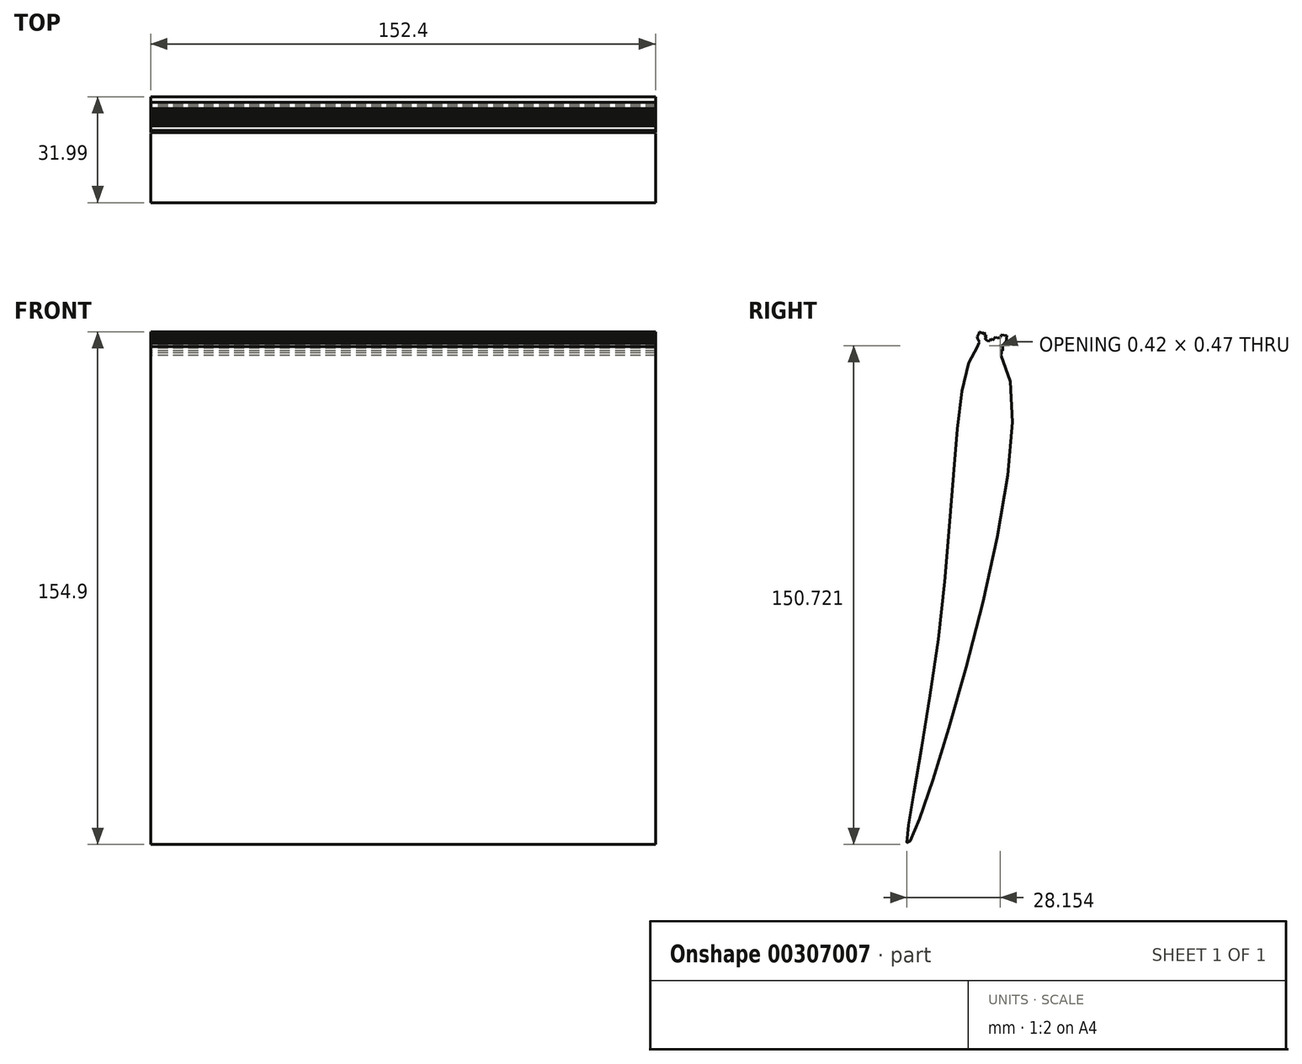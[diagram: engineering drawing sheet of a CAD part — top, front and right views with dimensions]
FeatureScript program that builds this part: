
annotation { "Feature Type Name" : "Feature", "Feature Type Description" : "" }
export const myFeature = defineFeature(function(context is Context, id is Id, definition is map)
    precondition{}
    {
        {
            var Q0;
            Q0=qCreatedBy(makeId("Right.planeOp"),FACE);
            var sketch = newSketch(context, id + "F0", { "sketchPlane" : qUnion([Q0])});
            skFitSpline(sketch, "E0", {"points": [v(19.1, 73.86) * mm, v(28.95, 59.3) * mm, v(-2.03, -76.46) * mm, v(7.39, -9.42) * mm, v(19.1, 73.86) * mm]});
            skLineSegment(sketch, "E1", {"start": v(23.21, 73.66) * mm, "end": v(25.8, 76.18) * mm});
            skLineSegment(sketch, "E2", {"start": v(25.8, 76.18) * mm, "end": v(26.77, 75.32) * mm});
            skLineSegment(sketch, "E3", {"start": v(26.77, 75.32) * mm, "end": v(24.37, 72.66) * mm});
            skLineSegment(sketch, "E4", {"start": v(24.37, 72.66) * mm, "end": v(23.21, 73.66) * mm});
            skLineSegment(sketch, "E5", {"start": v(25.8, 76.18) * mm, "end": v(26.45, 76.9) * mm});
            skPoint(sketch, "E5.endSnap0", {"position": v(26.29, 75.75) * mm});
            skLineSegment(sketch, "E6", {"start": v(26.45, 76.9) * mm, "end": v(27.35, 75.97) * mm});
            skLineSegment(sketch, "E7", {"start": v(27.35, 75.97) * mm, "end": v(26.77, 75.32) * mm});
            skLineSegment(sketch, "E8", {"start": v(20.8, 74.43) * mm, "end": v(20.13, 76.98) * mm});
            skLineSegment(sketch, "E9", {"start": v(20.13, 76.98) * mm, "end": v(18.88, 76.65) * mm});
            skLineSegment(sketch, "E10", {"start": v(18.88, 76.65) * mm, "end": v(19.55, 74.12) * mm});
            skLineSegment(sketch, "E11", {"start": v(19.55, 74.12) * mm, "end": v(20.8, 74.43) * mm});
            skLineSegment(sketch, "E12", {"start": v(24.94, 72.1) * mm, "end": v(25.14, 73.52) * mm});
            skLineSegment(sketch, "E13", {"start": v(25.14, 73.52) * mm, "end": v(25.57, 73.99) * mm});
            skLineSegment(sketch, "E14", {"start": v(25.57, 73.99) * mm, "end": v(25.53, 73.73) * mm});
            skPoint(sketch, "E14.endSnap0", {"position": v(25.35, 73.75) * mm});
            skLineSegment(sketch, "E15", {"start": v(25.53, 73.73) * mm, "end": v(25.14, 73.52) * mm});
            skLineSegment(sketch, "E16", {"start": v(25.04, 72.8) * mm, "end": v(25.73, 73.57) * mm});
            skLineSegment(sketch, "E17", {"start": v(25.73, 73.57) * mm, "end": v(25.83, 74.27) * mm});
            skLineSegment(sketch, "E18", {"start": v(25.83, 74.27) * mm, "end": v(26.25, 73.9) * mm});
            skLineSegment(sketch, "E19", {"start": v(26.25, 73.9) * mm, "end": v(25.73, 73.57) * mm});
            skLineSegment(sketch, "E20", {"start": v(26.43, 74.95) * mm, "end": v(27.27, 74.83) * mm});
            skLineSegment(sketch, "E21", {"start": v(27.27, 74.83) * mm, "end": v(26.77, 75.32) * mm});
            skLineSegment(sketch, "E22", {"start": v(27.35, 75.97) * mm, "end": v(27.33, 75.24) * mm});
            skLineSegment(sketch, "E23", {"start": v(27.33, 75.24) * mm, "end": v(26.65, 74.48) * mm});
            skLineSegment(sketch, "E24", {"start": v(26.65, 74.48) * mm, "end": v(25.83, 74.27) * mm});
            skLineSegment(sketch, "E25", {"start": v(26.65, 74.48) * mm, "end": v(26.6, 74.17) * mm});
            skLineSegment(sketch, "E26", {"start": v(26.6, 74.17) * mm, "end": v(26.25, 73.9) * mm});
            skLineSegment(sketch, "E27", {"start": v(27.33, 75.24) * mm, "end": v(26.77, 75.32) * mm});
            skLineSegment(sketch, "E28", {"start": v(26.25, 73.9) * mm, "end": v(26.1, 72.93) * mm});
            skLineSegment(sketch, "E29", {"start": v(26.1, 72.93) * mm, "end": v(25.04, 72.8) * mm});
            skLineSegment(sketch, "E30", {"start": v(27.35, 75.97) * mm, "end": v(27.46, 76.75) * mm});
            skLineSegment(sketch, "E31", {"start": v(27.46, 76.75) * mm, "end": v(27.04, 76.29) * mm});
            skLineSegment(sketch, "E32", {"start": v(27.04, 76.29) * mm, "end": v(27.46, 76.75) * mm});
            skLineSegment(sketch, "E33", {"start": v(27.46, 76.75) * mm, "end": v(26.45, 76.9) * mm});
            skLineSegment(sketch, "E34", {"start": v(26.45, 76.9) * mm, "end": v(25.63, 77) * mm});
            skLineSegment(sketch, "E35", {"start": v(25.63, 77) * mm, "end": v(25.52, 76.22) * mm});
            skLineSegment(sketch, "E36", {"start": v(25.52, 76.22) * mm, "end": v(24.54, 76) * mm});
            skLineSegment(sketch, "E37", {"start": v(24.54, 76) * mm, "end": v(24.06, 76.43) * mm});
            skLineSegment(sketch, "E38", {"start": v(24.06, 76.43) * mm, "end": v(23.9, 75.3) * mm});
            skLineSegment(sketch, "E39", {"start": v(23.9, 75.3) * mm, "end": v(23.84, 74.88) * mm});
            skLineSegment(sketch, "E40", {"start": v(23.84, 74.88) * mm, "end": v(23.1, 74.8) * mm});
            skLineSegment(sketch, "E41", {"start": v(23.1, 74.8) * mm, "end": v(22.98, 73.91) * mm});
            skLineSegment(sketch, "E42", {"start": v(22.98, 73.91) * mm, "end": v(23.21, 73.66) * mm});
            skLineSegment(sketch, "E43", {"start": v(24.06, 76.43) * mm, "end": v(23.14, 75.41) * mm});
            skLineSegment(sketch, "E44", {"start": v(23.14, 75.41) * mm, "end": v(22.6, 75.9) * mm});
            skLineSegment(sketch, "E45", {"start": v(22.6, 75.9) * mm, "end": v(22.24, 75.1) * mm});
            skLineSegment(sketch, "E46", {"start": v(22.24, 75.1) * mm, "end": v(21.53, 75.2) * mm});
            skLineSegment(sketch, "E47", {"start": v(21.53, 75.2) * mm, "end": v(21, 74.6) * mm});
            skLineSegment(sketch, "E48", {"start": v(21.53, 75.2) * mm, "end": v(20.95, 75.72) * mm});
            skLineSegment(sketch, "E49", {"start": v(20.95, 75.72) * mm, "end": v(20.6, 75.33) * mm});
            skLineSegment(sketch, "E50", {"start": v(20.6, 75.33) * mm, "end": v(20.72, 76.17) * mm});
            skLineSegment(sketch, "E51", {"start": v(20.72, 76.17) * mm, "end": v(20.24, 76.6) * mm});
            skLineSegment(sketch, "E52", {"start": v(20.24, 76.6) * mm, "end": v(20.13, 76.98) * mm});
            skLineSegment(sketch, "E53", {"start": v(20.72, 76.17) * mm, "end": v(20.82, 76.88) * mm});
            skLineSegment(sketch, "E54", {"start": v(20.82, 76.88) * mm, "end": v(20.24, 76.6) * mm});
            skLineSegment(sketch, "E55", {"start": v(20.82, 76.88) * mm, "end": v(21.3, 76.45) * mm});
            skLineSegment(sketch, "E56", {"start": v(21.3, 76.45) * mm, "end": v(20.72, 76.17) * mm});
            skLineSegment(sketch, "E57", {"start": v(20.82, 76.88) * mm, "end": v(20.6, 77.72) * mm});
            skLineSegment(sketch, "E58", {"start": v(20.6, 77.72) * mm, "end": v(20.13, 76.98) * mm});
            skLineSegment(sketch, "E59", {"start": v(20.13, 76.98) * mm, "end": v(19.6, 77.46) * mm});
            skPoint(sketch, "E59.endSnap0", {"position": v(19.5, 76.81) * mm});
            skLineSegment(sketch, "E60", {"start": v(19.6, 77.46) * mm, "end": v(18.88, 76.65) * mm});
            skLineSegment(sketch, "E61", {"start": v(18.88, 76.65) * mm, "end": v(19.06, 77.93) * mm});
            skLineSegment(sketch, "E62", {"start": v(19.06, 77.93) * mm, "end": v(20.37, 77.35) * mm});
            skLineSegment(sketch, "E63", {"start": v(20.37, 77.35) * mm, "end": v(20.6, 77.72) * mm});
            skLineSegment(sketch, "E64", {"start": v(18.95, 77.15) * mm, "end": v(18.36, 76.5) * mm});
            skLineSegment(sketch, "E65", {"start": v(18.36, 76.5) * mm, "end": v(19.28, 75.2) * mm});
            skLineSegment(sketch, "E66", {"start": v(19.28, 75.2) * mm, "end": v(18.63, 75.61) * mm});
            skLineSegment(sketch, "E67", {"start": v(18.63, 75.61) * mm, "end": v(18.5, 76.06) * mm});
            skLineSegment(sketch, "E68", {"start": v(18.5, 76.06) * mm, "end": v(18.36, 76.5) * mm});
            skLineSegment(sketch, "E69", {"start": v(19.55, 74.12) * mm, "end": v(19.1, 73.86) * mm});
            skLineSegment(sketch, "E70", {"start": v(19.1, 73.86) * mm, "end": v(18.92, 74.52) * mm});
            skLineSegment(sketch, "E71", {"start": v(18.92, 74.52) * mm, "end": v(19.34, 75.1) * mm});
            skLineSegment(sketch, "E72", {"start": v(19.34, 75.1) * mm, "end": v(18.63, 75.61) * mm});
            skLineSegment(sketch, "E73", {"start": v(18.63, 75.61) * mm, "end": v(19.13, 74.81) * mm});
            skLineSegment(sketch, "E74", {"start": v(26.1, 72.93) * mm, "end": v(26.19, 72.23) * mm});
            skLineSegment(sketch, "E75", {"start": v(26.19, 72.23) * mm, "end": v(25.67, 72.12) * mm});
            skLineSegment(sketch, "E76", {"start": v(25.67, 72.12) * mm, "end": v(25.82, 71.5) * mm});
            skLineSegment(sketch, "E77", {"start": v(25.82, 71.5) * mm, "end": v(25.72, 70.84) * mm});
            skLineSegment(sketch, "E78", {"start": v(25.72, 70.84) * mm, "end": v(24.94, 72.1) * mm});
            skLineSegment(sketch, "E79", {"start": v(18.92, 74.52) * mm, "end": v(18.53, 73.4) * mm});
            skLineSegment(sketch, "E80", {"start": v(18.53, 73.4) * mm, "end": v(19.1, 73.86) * mm});
            skLineSegment(sketch, "E81", {"start": v(20.72, 76.17) * mm, "end": v(20.95, 75.72) * mm});
            skLineSegment(sketch, "E82.0", {"start": v(18.92, 74.52) * mm, "end": v(25.73, 73.57) * mm, "construction": true});
            skLineSegment(sketch, "E83.0", {"start": v(18.5, 76.06) * mm, "end": v(27.27, 74.83) * mm, "construction": true});
            skLineSegment(sketch, "E84.0", {"start": v(18.63, 75.61) * mm, "end": v(21.53, 75.2) * mm, "construction": true});
            skLineSegment(sketch, "E85.0", {"start": v(19.28, 75.2) * mm, "end": v(26.6, 74.17) * mm, "construction": true});
            skLineSegment(sketch, "E86.0", {"start": v(18.36, 76.5) * mm, "end": v(27.33, 75.24) * mm, "construction": true});
            skLineSegment(sketch, "E87.0", {"start": v(19.06, 77.93) * mm, "end": v(27.46, 76.75) * mm, "construction": true});
            skLineSegment(sketch, "E88.0", {"start": v(18.95, 77.15) * mm, "end": v(27.35, 75.97) * mm, "construction": true});
            skLineSegment(sketch, "E89.0", {"start": v(20.24, 76.6) * mm, "end": v(26.29, 75.75) * mm, "construction": true});
            skLineSegment(sketch, "E90.0", {"start": v(25.35, 73.75) * mm, "end": v(25.53, 73.73) * mm, "construction": true});
            skLineSegment(sketch, "E91.0", {"start": v(23.14, 75.41) * mm, "end": v(23.9, 75.3) * mm, "construction": true});
            skLineSegment(sketch, "E92.0", {"start": v(23.84, 74.88) * mm, "end": v(26.65, 74.48) * mm, "construction": true});
            skLineSegment(sketch, "E93.0", {"start": v(19.28, 75.2) * mm, "end": v(19.6, 77.46) * mm, "construction": true});
            skLineSegment(sketch, "E94.0", {"start": v(26.65, 74.48) * mm, "end": v(26.77, 75.32) * mm, "construction": true});
            skLineSegment(sketch, "E95.0", {"start": v(18.88, 76.65) * mm, "end": v(18.95, 77.15) * mm, "construction": true});
            skLineSegment(sketch, "E96.0", {"start": v(26.29, 75.75) * mm, "end": v(26.45, 76.9) * mm, "construction": true});
            skLineSegment(sketch, "E97.0", {"start": v(25.04, 72.8) * mm, "end": v(25.63, 77) * mm, "construction": true});
            skLineSegment(sketch, "E98.0", {"start": v(27.27, 74.83) * mm, "end": v(27.33, 75.24) * mm, "construction": true});
            skSolve(sketch);
        }
        {
            var Q0;
            Q0=qSketchRegion(id+"F0",true);
            var Q1;
            Q1=makeQuery(id+"F0.imprint","IMPRINT",FACE,{"disambiguationData":[TD([[makeQuery(id+"F0.imprint","IMPRINT",EDGE,{"derivedFrom":sQuery(id+"F0.wireOp",EDGE,"E1")}),1.0]])]});
            var Q2;
            {var subQ3=sQuery(id+"F0.wireOp",EDGE,"E1");Q2=makeQuery(id+"F0.imprint","IMPRINT",FACE,{"disambiguationData":[TD([[makeQuery(id+"F0.imprint","IMPRINT",EDGE,{"derivedFrom":subQ3}),-1.0]])]});}
            var Q3;
            {var subQ0=sQuery(id+"F0.wireOp",EDGE,"E29");Q3=makeQuery(id+"F0.imprint","IMPRINT",FACE,{"disambiguationData":[TD([[makeQuery(id+"F0.imprint","IMPRINT",EDGE,{"derivedFrom":subQ0}),1.0]])]});}
            var Q4;
            {var subQ0=sQuery(id+"F0.wireOp",EDGE,"E78");var subQ1=sQuery(id+"F0.wireOp",EDGE,"E12");var subQ2=makeQuery(id+"F0.imprint","INTERSECT",VERTEX,{"derivedFrom":[subQ1,subQ0]});Q4=makeQuery(id+"F0.imprint","IMPRINT",FACE,{"disambiguationData":[TD([[makeQuery(id+"F0.imprint","IMPRINT",EDGE,{"disambiguationData":[TD([[subQ2,1.0]])],"derivedFrom":subQ0}),1.0]])]});}
            var Q5;
            {var subQ2=sQuery(id+"F0.wireOp",EDGE,"E8");Q5=makeQuery(id+"F0.imprint","IMPRINT",FACE,{"disambiguationData":[TD([[makeQuery(id+"F0.imprint","IMPRINT",EDGE,{"derivedFrom":subQ2}),-1.0]])]});}
            var Q6;
            {var subQ0=sQuery(id+"F0.wireOp",EDGE,"E11");Q6=makeQuery(id+"F0.imprint","IMPRINT",FACE,{"disambiguationData":[TD([[makeQuery(id+"F0.imprint","IMPRINT",EDGE,{"derivedFrom":subQ0}),1.0]])]});}
            var Q7;
            {var subQ0=sQuery(id+"F0.wireOp",EDGE,"E4");Q7=makeQuery(id+"F0.imprint","IMPRINT",FACE,{"disambiguationData":[TD([[makeQuery(id+"F0.imprint","IMPRINT",EDGE,{"derivedFrom":subQ0}),-1.0]])]});}
            var Q8;
            {var subQ0=sQuery(id+"F0.wireOp",EDGE,"E78");var subQ1=sQuery(id+"F0.wireOp",EDGE,"E0");var subQ3=makeQuery(id+"F0.imprint","INTERSECT",VERTEX,{"derivedFrom":[subQ1,subQ0]});Q8=makeQuery(id+"F0.imprint","IMPRINT",FACE,{"disambiguationData":[TD([[makeQuery(id+"F0.imprint","IMPRINT",EDGE,{"disambiguationData":[TD([[subQ3,-1.0]])],"derivedFrom":subQ1}),-1.0]])]});}
            var Q9;
            {var subQ6=sQuery(id+"F0.wireOp",EDGE,"E8");Q9=makeQuery(id+"F0.imprint","IMPRINT",FACE,{"disambiguationData":[TD([[makeQuery(id+"F0.imprint","IMPRINT",EDGE,{"derivedFrom":subQ6}),1.0]])]});}
            var Q10;
            Q10=makeQuery(id+"F0.imprint","IMPRINT",FACE,{"disambiguationData":[TD([[makeQuery(id+"F0.imprint","IMPRINT",EDGE,{"derivedFrom":sQuery(id+"F0.wireOp",EDGE,"E58")}),-1.0]])]});
            var Q11;
            {var subQ0=sQuery(id+"F0.wireOp",EDGE,"E69");Q11=makeQuery(id+"F0.imprint","IMPRINT",FACE,{"disambiguationData":[TD([[makeQuery(id+"F0.imprint","IMPRINT",EDGE,{"derivedFrom":subQ0}),-1.0]])]});}
            var Q12;
            {var subQ1=sQuery(id+"F0.wireOp",EDGE,"E70");Q12=makeQuery(id+"F0.imprint","IMPRINT",FACE,{"disambiguationData":[TD([[makeQuery(id+"F0.imprint","IMPRINT",EDGE,{"derivedFrom":subQ1}),1.0]])]});}
            var Q13;
            {var subQ0=sQuery(id+"F0.wireOp",EDGE,"E80");Q13=makeQuery(id+"F0.imprint","IMPRINT",FACE,{"disambiguationData":[TD([[makeQuery(id+"F0.imprint","IMPRINT",EDGE,{"derivedFrom":subQ0}),1.0]])]});}
            var Q14;
            {var subQ5=sQuery(id+"F0.wireOp",EDGE,"E64");Q14=makeQuery(id+"F0.imprint","IMPRINT",FACE,{"disambiguationData":[TD([[makeQuery(id+"F0.imprint","IMPRINT",EDGE,{"derivedFrom":subQ5}),1.0]])]});}
            var Q15;
            {var subQ1=sQuery(id+"F0.wireOp",EDGE,"E70");Q15=makeQuery(id+"F0.imprint","IMPRINT",FACE,{"disambiguationData":[TD([[makeQuery(id+"F0.imprint","IMPRINT",EDGE,{"derivedFrom":subQ1}),-1.0]])]});}
            var Q16;
            {var subQ0=sQuery(id+"F0.wireOp",EDGE,"E67");Q16=makeQuery(id+"F0.imprint","IMPRINT",FACE,{"disambiguationData":[TD([[makeQuery(id+"F0.imprint","IMPRINT",EDGE,{"derivedFrom":subQ0}),-1.0]])]});}
            var Q17;
            {var subQ0=sQuery(id+"F0.wireOp",EDGE,"E72");var subQ1=sQuery(id+"F0.wireOp",EDGE,"E10");var subQ2=makeQuery(id+"F0.imprint","INTERSECT",VERTEX,{"derivedFrom":[subQ1,subQ0]});Q17=makeQuery(id+"F0.imprint","IMPRINT",FACE,{"disambiguationData":[TD([[makeQuery(id+"F0.imprint","IMPRINT",EDGE,{"disambiguationData":[TD([[subQ2,-1.0]])],"derivedFrom":subQ1}),1.0]])]});}
            var Q18;
            Q18=makeQuery(id+"F0.imprint","IMPRINT",FACE,{"disambiguationData":[TD([[makeQuery(id+"F0.imprint","IMPRINT",EDGE,{"derivedFrom":sQuery(id+"F0.wireOp",EDGE,"E9")}),-1.0]])]});
            var Q19;
            Q19=makeQuery(id+"F0.imprint","IMPRINT",FACE,{"disambiguationData":[TD([[makeQuery(id+"F0.imprint","IMPRINT",EDGE,{"derivedFrom":sQuery(id+"F0.wireOp",EDGE,"E17")}),-1.0]])]});
            var Q20;
            {var subQ0=sQuery(id+"F0.wireOp",EDGE,"E65");var subQ1=sQuery(id+"F0.wireOp",EDGE,"E10");var subQ2=makeQuery(id+"F0.imprint","INTERSECT",VERTEX,{"derivedFrom":[subQ1,subQ0]});Q20=makeQuery(id+"F0.imprint","IMPRINT",FACE,{"disambiguationData":[TD([[makeQuery(id+"F0.imprint","IMPRINT",EDGE,{"disambiguationData":[TD([[subQ2,-1.0]])],"derivedFrom":subQ1}),1.0]])]});}
            var Q21;
            Q21=makeQuery(id+"F0.imprint","IMPRINT",FACE,{"disambiguationData":[TD([[makeQuery(id+"F0.imprint","IMPRINT",EDGE,{"derivedFrom":sQuery(id+"F0.wireOp",EDGE,"E18")}),1.0]])]});
            var Q22;
            Q22=makeQuery(id+"F0.imprint","IMPRINT",FACE,{"disambiguationData":[TD([[makeQuery(id+"F0.imprint","IMPRINT",EDGE,{"derivedFrom":sQuery(id+"F0.wireOp",EDGE,"E49")}),-1.0]])]});
            var Q23;
            {var subQ2=sQuery(id+"F0.wireOp",EDGE,"E32");Q23=makeQuery(id+"F0.imprint","IMPRINT",FACE,{"disambiguationData":[TD([[makeQuery(id+"F0.imprint","IMPRINT",EDGE,{"derivedFrom":subQ2}),1.0]])]});}
            var Q24;
            {var subQ0=sQuery(id+"F0.wireOp",EDGE,"E66");var subQ1=sQuery(id+"F0.wireOp",EDGE,"E10");var subQ2=makeQuery(id+"F0.imprint","INTERSECT",VERTEX,{"derivedFrom":[subQ1,subQ0]});Q24=makeQuery(id+"F0.imprint","IMPRINT",FACE,{"disambiguationData":[TD([[makeQuery(id+"F0.imprint","IMPRINT",EDGE,{"disambiguationData":[TD([[subQ2,-1.0]])],"derivedFrom":subQ1}),-1.0]])]});}
            var Q25;
            Q25=makeQuery(id+"F0.imprint","IMPRINT",FACE,{"disambiguationData":[TD([[makeQuery(id+"F0.imprint","IMPRINT",EDGE,{"derivedFrom":sQuery(id+"F0.wireOp",EDGE,"E2")}),1.0]])]});
            var Q26;
            {var subQ5=sQuery(id+"F0.wireOp",EDGE,"E73");Q26=makeQuery(id+"F0.imprint","IMPRINT",FACE,{"disambiguationData":[TD([[makeQuery(id+"F0.imprint","IMPRINT",EDGE,{"derivedFrom":subQ5}),1.0]])]});}
            var Q27;
            {var subQ1=sQuery(id+"F0.wireOp",EDGE,"E14");Q27=makeQuery(id+"F0.imprint","IMPRINT",FACE,{"disambiguationData":[TD([[makeQuery(id+"F0.imprint","IMPRINT",EDGE,{"derivedFrom":subQ1}),1.0]])]});}
            var Q28;
            Q28=makeQuery(id+"F0.imprint","IMPRINT",FACE,{"disambiguationData":[TD([[makeQuery(id+"F0.imprint","IMPRINT",EDGE,{"derivedFrom":sQuery(id+"F0.wireOp",EDGE,"E16")}),-1.0]])]});
            var Q29;
            {var subQ0=sQuery(id+"F0.wireOp",EDGE,"E24");Q29=makeQuery(id+"F0.imprint","IMPRINT",FACE,{"disambiguationData":[TD([[makeQuery(id+"F0.imprint","IMPRINT",EDGE,{"derivedFrom":subQ0}),-1.0]])]});}
            var Q30;
            Q30=makeQuery(id+"F0.imprint","IMPRINT",FACE,{"disambiguationData":[TD([[makeQuery(id+"F0.imprint","IMPRINT",EDGE,{"derivedFrom":sQuery(id+"F0.wireOp",EDGE,"E13")}),-1.0]])]});
            var Q31;
            {var subQ0=sQuery(id+"F0.wireOp",EDGE,"E21");var subQ1=sQuery(id+"F0.wireOp",EDGE,"E20");var subQ2=makeQuery(id+"F0.imprint","INTERSECT",VERTEX,{"derivedFrom":[subQ1,subQ0]});Q31=makeQuery(id+"F0.imprint","IMPRINT",FACE,{"disambiguationData":[TD([[makeQuery(id+"F0.imprint","IMPRINT",EDGE,{"disambiguationData":[TD([[subQ2,1.0]])],"derivedFrom":subQ1}),1.0]])]});}
            var Q32;
            Q32=makeQuery(id+"F0.imprint","IMPRINT",FACE,{"disambiguationData":[TD([[makeQuery(id+"F0.imprint","IMPRINT",EDGE,{"derivedFrom":sQuery(id+"F0.wireOp",EDGE,"E53")}),-1.0]])]});
            var Q33;
            {var subQ0=sQuery(id+"F0.wireOp",EDGE,"E30");Q33=makeQuery(id+"F0.imprint","IMPRINT",FACE,{"disambiguationData":[TD([[makeQuery(id+"F0.imprint","IMPRINT",EDGE,{"derivedFrom":subQ0}),1.0]])]});}
            var Q34;
            Q34=makeQuery(id+"F0.imprint","IMPRINT",FACE,{"disambiguationData":[TD([[makeQuery(id+"F0.imprint","IMPRINT",EDGE,{"derivedFrom":sQuery(id+"F0.wireOp",EDGE,"E7")}),1.0]])]});
            var Q35;
            Q35=makeQuery(id+"F0.imprint","IMPRINT",FACE,{"disambiguationData":[TD([[makeQuery(id+"F0.imprint","IMPRINT",EDGE,{"derivedFrom":sQuery(id+"F0.wireOp",EDGE,"E51")}),-1.0]])]});
            var Q36;
            Q36=makeQuery(id+"F0.imprint","IMPRINT",FACE,{"disambiguationData":[TD([[makeQuery(id+"F0.imprint","IMPRINT",EDGE,{"derivedFrom":sQuery(id+"F0.wireOp",EDGE,"E52")}),-1.0]])]});
            var Q37;
            {var subQ1=sQuery(id+"F0.wireOp",EDGE,"E3");var subQ3=sQuery(id+"F0.wireOp",EDGE,"E20");var subQ4=makeQuery(id+"F0.imprint","INTERSECT",VERTEX,{"derivedFrom":[subQ1,subQ3]});Q37=makeQuery(id+"F0.imprint","IMPRINT",FACE,{"disambiguationData":[TD([[makeQuery(id+"F0.imprint","IMPRINT",EDGE,{"disambiguationData":[TD([[subQ4,-1.0]])],"derivedFrom":subQ3}),1.0]])]});}
            var Q38;
            {var subQ0=sQuery(id+"F0.wireOp",EDGE,"E27");Q38=makeQuery(id+"F0.imprint","IMPRINT",FACE,{"disambiguationData":[TD([[makeQuery(id+"F0.imprint","IMPRINT",EDGE,{"derivedFrom":subQ0}),1.0]])]});}
            var Q39;
            {var subQ4=sQuery(id+"F0.wireOp",EDGE,"E4");Q39=makeQuery(id+"F0.imprint","IMPRINT",FACE,{"disambiguationData":[TD([[makeQuery(id+"F0.imprint","IMPRINT",EDGE,{"derivedFrom":subQ4}),1.0]])]});}
            extrude(context, id + "F1", {"entities" : qUnion([Q0, Q1, Q2, Q3, Q4, Q5, Q6, Q7, Q8, Q9, Q10, Q11, Q12, Q13, Q14, Q15, Q16, Q17, Q18, Q19, Q20, Q21, Q22, Q23, Q24, Q25, Q26, Q27, Q28, Q29, Q30, Q31, Q32, Q33, Q34, Q35, Q36, Q37, Q38, Q39]), "depth" : 76.2 * mm, "hasSecondDirection" : true, "secondDirectionOppositeDirection" : true, "secondDirectionDepth" : 76.2 * mm});
        }
    });
